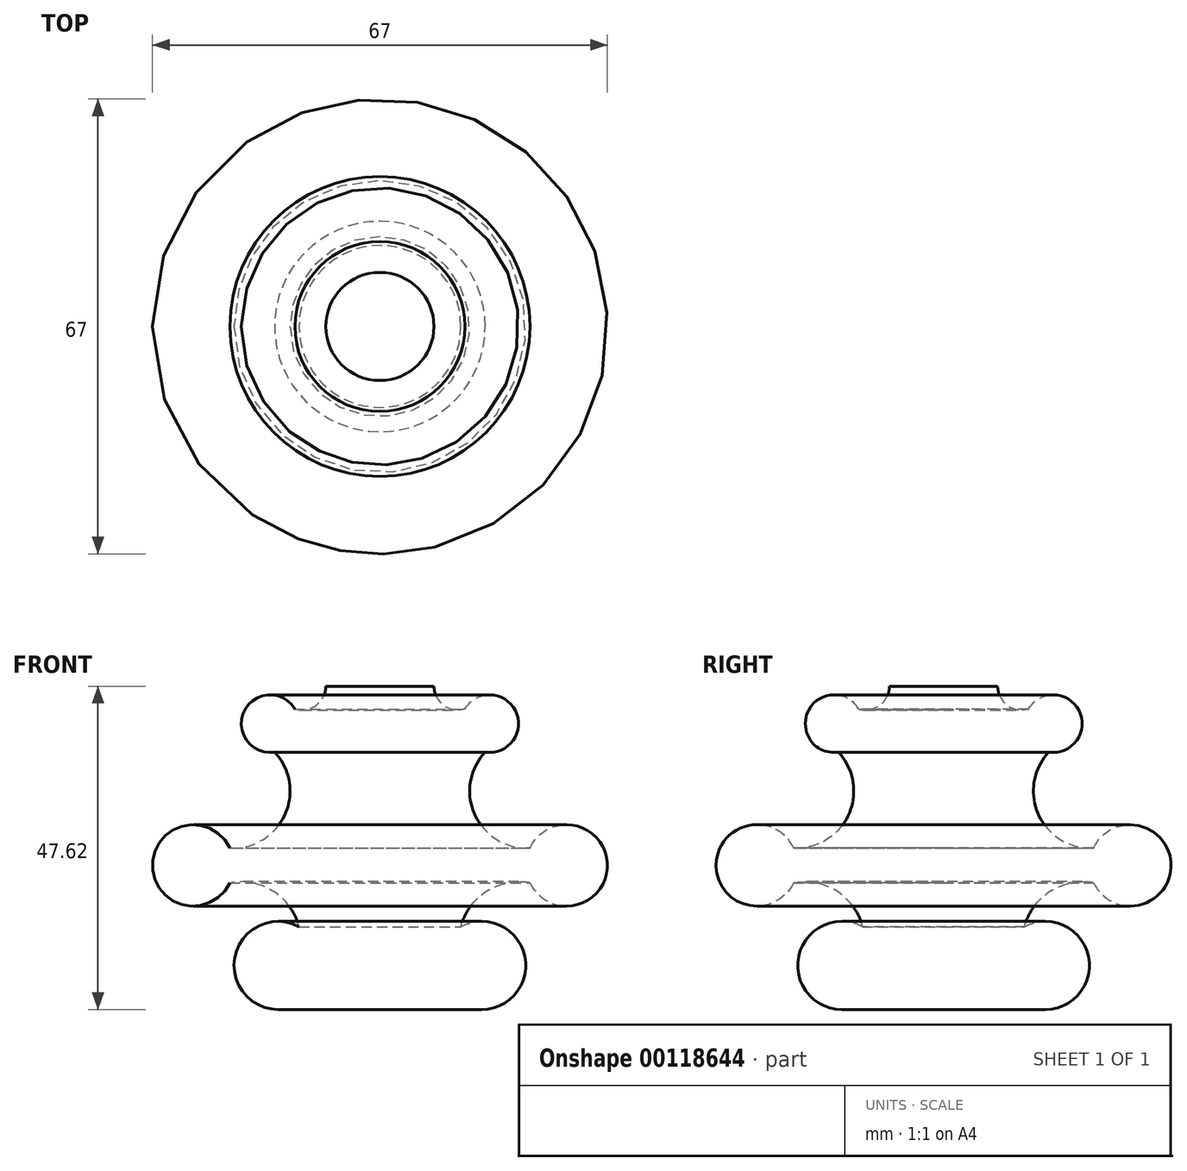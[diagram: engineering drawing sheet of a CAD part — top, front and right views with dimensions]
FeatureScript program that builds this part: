
annotation { "Feature Type Name" : "Feature", "Feature Type Description" : "" }
export const myFeature = defineFeature(function(context is Context, id is Id, definition is map)
    precondition{}
    {
        {
            var Q0;
            Q0=qCreatedBy(makeId("Front.planeOp"),FACE);
            var sketch = newSketch(context, id + "F0", { "sketchPlane" : qUnion([Q0])});
            skLineSegment(sketch, "E0", {"start": v(0, 0) * mm, "end": v(15, 0) * mm});
            skLineSegment(sketch, "E1", {"start": v(0, 0) * mm, "end": v(0, 50) * mm});
            skArc(sketch, "E2", {"start": v(7.97, 47.62) * mm, "mid": v(5.58, 54.16) * mm, "end": v(0, 50) * mm});
            skArc(sketch, "E3", {"start": v(7.97, 47.62) * mm, "mid": v(9.4, 44.8) * mm, "end": v(12.51, 44.26) * mm});
            skArc(sketch, "E4", {"start": v(15.5, 37.92) * mm, "mid": v(20, 43.92) * mm, "end": v(12.51, 44.26) * mm});
            skArc(sketch, "E5", {"start": v(15.5, 37.92) * mm, "mid": v(14, 28.63) * mm, "end": v(22.09, 23.8) * mm});
            skArc(sketch, "E6", {"start": v(22.09, 18.65) * mm, "mid": v(15.73, 17.43) * mm, "end": v(11.92, 12.19) * mm});
            skArc(sketch, "E7", {"start": v(22.09, 18.65) * mm, "mid": v(33.5, 21.23) * mm, "end": v(22.09, 23.8) * mm});
            skArc(sketch, "E8", {"start": v(15, 0) * mm, "mid": v(21.28, 8.07) * mm, "end": v(11.92, 12.19) * mm});
            skSolve(sketch);
        }
        {
            var Q0;
            Q0=makeQuery(id+"F0.imprint","IMPRINT",FACE,{"disambiguationData":[TD([[makeQuery(id+"F0.imprint","IMPRINT",EDGE,{"derivedFrom":sQuery(id+"F0.wireOp",EDGE,"E0")}),1.0]])]});
            var Q1;
            Q1=sQuery(id+"F0.wireOp",EDGE,"E1");
            revolve(context, id + "F1", {"entities" : qUnion([Q0]), "axis" : qUnion([Q1]), "revolveType" : RevolveType.FULL});
        }
    });
